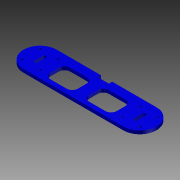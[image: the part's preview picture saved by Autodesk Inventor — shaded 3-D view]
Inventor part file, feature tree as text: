
AUTODESK INVENTOR PART (.ipt)
format: ipt  version: 2012 (Build 160160000, 160)  size: 147,456 bytes
history: native  units: mm
features: extrude x1, sketch x1
ambient origin geometry x8: Origin, YZ Plane, XZ Plane, XY Plane, X Axis, Y Axis, Z Axis, Center Point
feature tree (2):
  extrude  "Extrusion4"  Depth=120.0mm
  sketch  "Sketch1"  dims[d0=30.0mm d1=120.0mm d2=10.0mm d3=3.0mm d4=13.5mm d5=10.0mm d6=87.0mm d7=3.0mm d8=10.0mm d9=10.0mm d10=15.0mm d11=10.0mm d12=55.0mm d13=3.0mm d16=5.0mm d17=5.0mm d18=30.0mm d19=30.0mm d20=5.0mm d23=25.0mm d24=25.0mm d25=5.0mm d27=8.0mm d30=2.0mm d31=8.132mm d32=8.132mm d33=40.0mm d35=360.0deg d37=2.0mm d40=8.132mm d41=8.132mm d42=40.0mm d44=360.0deg d46=3.0mm d47=0.0mm d48=18.0mm d50=3.0mm d51=15.0mm]
